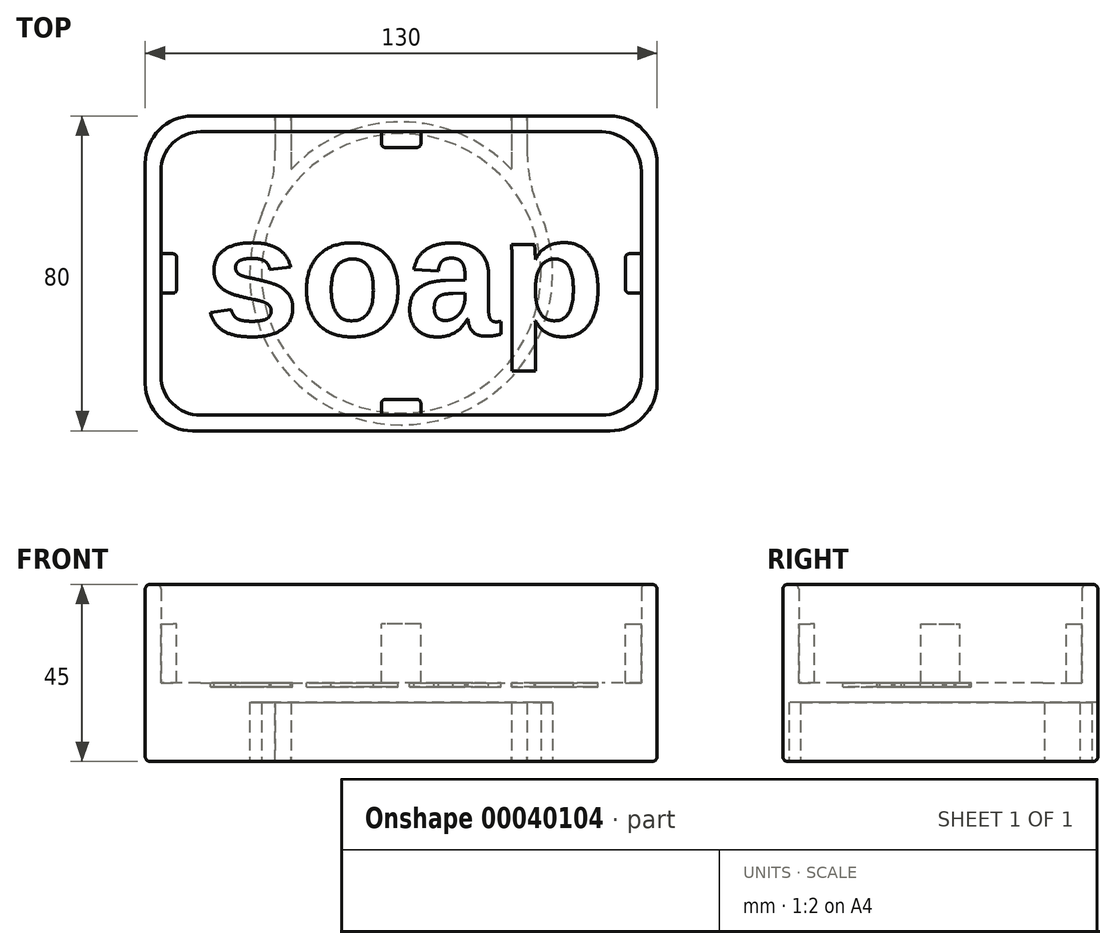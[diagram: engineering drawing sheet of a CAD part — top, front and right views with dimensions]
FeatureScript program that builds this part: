
annotation { "Feature Type Name" : "Feature", "Feature Type Description" : "" }
export const myFeature = defineFeature(function(context is Context, id is Id, definition is map)
    precondition{}
    {
        {
            assignVariable(context, id + "F0", {"name" : "long", "anyValue" : 130});
        }
        {
            assignVariable(context, id + "F1", {"name" : "large", "anyValue" : 80});
        }
        {
            var Q0;
            Q0=qCreatedBy(makeId("Top.planeOp"),FACE);
            var sketch = newSketch(context, id + "F2", { "sketchPlane" : qUnion([Q0])});
            skLineSegment(sketch, "E0.bottom", {"start": v(0, 0) * mm, "end": v(130, 0) * mm});
            skLineSegment(sketch, "E0.top", {"start": v(0, 80) * mm, "end": v(130, 80) * mm});
            skLineSegment(sketch, "E0.left", {"start": v(0, 0) * mm, "end": v(0, 80) * mm});
            skLineSegment(sketch, "E0.right", {"start": v(130, 0) * mm, "end": v(130, 80) * mm});
            skSolve(sketch);
        }
        {
            var Q0;
            Q0 = qSketchRegion(id + "F2", true);
            extrude(context, id + "F3", {"entities" : qUnion([Q0]), "depth" : 20 * mm});
        }
        {
            var Q0;
            Q0=makeQuery(id+"F3.opExtrude","CAP_FACE",FACE,{"disambiguationData":[OSD([sQuery(id+"F2.wireOp",EDGE,"E0.bottom"),sQuery(id+"F2.wireOp",EDGE,"E0.top"),sQuery(id+"F2.wireOp",EDGE,"E0.left"),sQuery(id+"F2.wireOp",EDGE,"E0.right")])],"isStart":true});
            var sketch = newSketch(context, id + "F4", { "sketchPlane" : qUnion([Q0])});
            skPoint(sketch, "E1", {"position": v(65, -80) * mm});
            skPoint(sketch, "E2", {"position": v(65, 0) * mm});
            skLineSegment(sketch, "E3", {"start": v(65, -80) * mm, "end": v(65, 0) * mm, "construction": true});
            skPoint(sketch, "E4", {"position": v(65, -40) * mm});
            skCircle(sketch, "E5", {"center": v(65, -40) * mm, "radius": 35.5 * mm});
            skCircle(sketch, "E6", {"center": v(65, -40) * mm, "radius": 38.5 * mm});
            skPoint(sketch, "E7", {"position": v(93, -80) * mm});
            skLineSegment(sketch, "E8.bottom", {"start": v(93, -80) * mm, "end": v(97, -80) * mm});
            skLineSegment(sketch, "E8.top", {"start": v(93, -61.4) * mm, "end": v(97, -61.4) * mm});
            skLineSegment(sketch, "E8.left", {"start": v(93, -80) * mm, "end": v(93, -61.4) * mm});
            skLineSegment(sketch, "E8.right", {"start": v(97, -80) * mm, "end": v(97, -61.4) * mm});
            skLineSegment(sketch, "E9.bottom", {"start": v(37, -80) * mm, "end": v(33, -80) * mm});
            skLineSegment(sketch, "E9.top", {"start": v(37, -61.4) * mm, "end": v(33, -61.4) * mm});
            skLineSegment(sketch, "E9.left", {"start": v(37, -80) * mm, "end": v(37, -61.4) * mm});
            skLineSegment(sketch, "E9.right", {"start": v(33, -80) * mm, "end": v(33, -61.4) * mm});
            skSolve(sketch);
        }
        {
            var Q0;
            Q0 = qSketchRegion(id + "F4", true);
            extrude(context, id + "F5", {"entities" : qUnion([Q0]), "operationType" : NewBodyOperationType.REMOVE, "oppositeDirection" : true, "depth" : 15 * mm});
        }
        {
            var Q0;
            Q0=makeQuery(id+"F3.opExtrude","CAP_FACE",FACE,{"disambiguationData":[OSD([sQuery(id+"F2.wireOp",EDGE,"E0.bottom"),sQuery(id+"F2.wireOp",EDGE,"E0.top"),sQuery(id+"F2.wireOp",EDGE,"E0.left"),sQuery(id+"F2.wireOp",EDGE,"E0.right")])],"isStart":false});
            var sketch = newSketch(context, id + "F6", { "sketchPlane" : qUnion([Q0])});
            skLineSegment(sketch, "E10.bottom", {"start": v(0, 80) * mm, "end": v(130, 80) * mm});
            skLineSegment(sketch, "E10.top", {"start": v(0, 0) * mm, "end": v(130, 0) * mm});
            skLineSegment(sketch, "E10.left", {"start": v(0, 80) * mm, "end": v(0, 0) * mm});
            skLineSegment(sketch, "E10.right", {"start": v(130, 80) * mm, "end": v(130, 0) * mm});
            skLineSegment(sketch, "E11.bottom", {"start": v(4, 76) * mm, "end": v(126, 76) * mm});
            skLineSegment(sketch, "E11.top", {"start": v(4, 4) * mm, "end": v(126, 4) * mm});
            skLineSegment(sketch, "E11.left", {"start": v(4, 76) * mm, "end": v(4, 4) * mm});
            skLineSegment(sketch, "E11.right", {"start": v(126, 76) * mm, "end": v(126, 4) * mm});
            skSolve(sketch);
        }
        {
            var Q0;
            Q0 = qSketchRegion(id + "F6", true);
            extrude(context, id + "F7", {"entities" : qUnion([Q0]), "operationType" : NewBodyOperationType.ADD, "depth" : 25 * mm});
        }
        {
            var Q0;
            Q0=makeQuery(id+"F7.opExtrude","SWEPT_EDGE",EDGE,{"disambiguationData":[OSD([sQuery(id+"F6.wireOp",EDGE,"E11.bottom"),sQuery(id+"F6.wireOp",EDGE,"E11.left")])]});
            var Q1;
            Q1=makeQuery(id+"F7.opExtrude","SWEPT_EDGE",EDGE,{"disambiguationData":[OSD([sQuery(id+"F6.wireOp",EDGE,"E11.bottom"),sQuery(id+"F6.wireOp",EDGE,"E11.right")])]});
            var Q2;
            Q2=makeQuery(id+"F7.opExtrude","SWEPT_EDGE",EDGE,{"disambiguationData":[OSD([sQuery(id+"F6.wireOp",EDGE,"E11.top"),sQuery(id+"F6.wireOp",EDGE,"E11.right")])]});
            var Q3;
            Q3=makeQuery(id+"F7.opExtrude","SWEPT_EDGE",EDGE,{"disambiguationData":[OSD([sQuery(id+"F6.wireOp",EDGE,"E11.top"),sQuery(id+"F6.wireOp",EDGE,"E11.left")])]});
            fillet(context, id + "F8", {"entities" : qUnion([Q0, Q1, Q2, Q3]), "radius" : 10 * mm, "tangentPropagation" : true, "allowEdgeOverflow" : false});
        }
        {
            var Q0;
            Q0=makeQuery(id+"F7.boolean.opBoolean","MERGE",EDGE,{"derivedFrom":[makeQuery(id+"F3.opExtrude","SWEPT_EDGE",EDGE,{"disambiguationData":[OSD([sQuery(id+"F2.wireOp",EDGE,"E0.top"),sQuery(id+"F2.wireOp",EDGE,"E0.left")])]}),makeQuery(id+"F7.opExtrude","SWEPT_EDGE",EDGE,{"disambiguationData":[OSD([sQuery(id+"F6.wireOp",EDGE,"E10.bottom"),sQuery(id+"F6.wireOp",EDGE,"E10.left")])]})]});
            var Q1;
            Q1=makeQuery(id+"F7.boolean.opBoolean","MERGE",EDGE,{"derivedFrom":[makeQuery(id+"F3.opExtrude","SWEPT_EDGE",EDGE,{"disambiguationData":[OSD([sQuery(id+"F2.wireOp",EDGE,"E0.bottom"),sQuery(id+"F2.wireOp",EDGE,"E0.left")])]}),makeQuery(id+"F7.opExtrude","SWEPT_EDGE",EDGE,{"disambiguationData":[OSD([sQuery(id+"F6.wireOp",EDGE,"E10.top"),sQuery(id+"F6.wireOp",EDGE,"E10.left")])]})]});
            var Q2;
            Q2=makeQuery(id+"F7.boolean.opBoolean","MERGE",EDGE,{"derivedFrom":[makeQuery(id+"F3.opExtrude","SWEPT_EDGE",EDGE,{"disambiguationData":[OSD([sQuery(id+"F2.wireOp",EDGE,"E0.bottom"),sQuery(id+"F2.wireOp",EDGE,"E0.right")])]}),makeQuery(id+"F7.opExtrude","SWEPT_EDGE",EDGE,{"disambiguationData":[OSD([sQuery(id+"F6.wireOp",EDGE,"E10.top"),sQuery(id+"F6.wireOp",EDGE,"E10.right")])]})]});
            var Q3;
            Q3=makeQuery(id+"F7.boolean.opBoolean","MERGE",EDGE,{"derivedFrom":[makeQuery(id+"F3.opExtrude","SWEPT_EDGE",EDGE,{"disambiguationData":[OSD([sQuery(id+"F2.wireOp",EDGE,"E0.top"),sQuery(id+"F2.wireOp",EDGE,"E0.right")])]}),makeQuery(id+"F7.opExtrude","SWEPT_EDGE",EDGE,{"disambiguationData":[OSD([sQuery(id+"F6.wireOp",EDGE,"E10.bottom"),sQuery(id+"F6.wireOp",EDGE,"E10.right")])]})]});
            fillet(context, id + "F9", {"entities" : qUnion([Q0, Q1, Q2, Q3]), "radius" : 12 * mm, "tangentPropagation" : true, "allowEdgeOverflow" : false});
        }
        {
            var Q0;
            Q0=qCreatedBy(makeId("Right.planeOp"),FACE);
            cPlane(context, id + "F10", {"entities" : qUnion([Q0]), "cplaneType" : CPlaneType.OFFSET, "offset" : (getVariable(context, 'long') / 2) * mm, "width" : 150 * mm, "height" : 150 * mm});
        }
        {
            var Q0;
            Q0=qCreatedBy(id+"F10.planeOp",FACE);
            var sketch = newSketch(context, id + "F11", { "sketchPlane" : qUnion([Q0])});
            skLineSegment(sketch, "E12.bottom", {"start": v(4, 20) * mm, "end": v(8, 20) * mm});
            skLineSegment(sketch, "E12.top", {"start": v(4, 35) * mm, "end": v(8, 35) * mm});
            skLineSegment(sketch, "E12.left", {"start": v(4, 20) * mm, "end": v(4, 35) * mm});
            skLineSegment(sketch, "E12.right", {"start": v(8, 20) * mm, "end": v(8, 35) * mm});
            skLineSegment(sketch, "E13.1.0.0", {"start": v(72, 20) * mm, "end": v(72, 35) * mm});
            skLineSegment(sketch, "E13.1.0.1", {"start": v(76, 20) * mm, "end": v(76, 35) * mm});
            skLineSegment(sketch, "E13.1.0.2", {"start": v(72, 20) * mm, "end": v(76, 20) * mm});
            skLineSegment(sketch, "E13.1.0.3", {"start": v(72, 35) * mm, "end": v(76, 35) * mm});
            skLineSegment(sketch, "E13.direction1", {"start": v(4, 20) * mm, "end": v(72, 20) * mm, "construction": true});
            skSolve(sketch);
        }
        {
            var Q0;
            Q0 = qSketchRegion(id + "F11", true);
            extrude(context, id + "F12", {"entities" : qUnion([Q0]), "operationType" : NewBodyOperationType.ADD, "endBound" : BoundingType.SYMMETRIC, "depth" : 10 * mm});
        }
        {
            var Q0;
            Q0=qCreatedBy(makeId("Front.planeOp"),FACE);
            cPlane(context, id + "F13", {"entities" : qUnion([Q0]), "cplaneType" : CPlaneType.OFFSET, "offset" : (getVariable(context, 'large') / 2) * mm, "oppositeDirection" : true, "width" : 150 * mm, "height" : 150 * mm});
        }
        {
            var Q0;
            Q0=qCreatedBy(id+"F13.planeOp",FACE);
            var sketch = newSketch(context, id + "F14", { "sketchPlane" : qUnion([Q0])});
            skLineSegment(sketch, "E14.bottom", {"start": v(4, 20) * mm, "end": v(8, 20) * mm});
            skLineSegment(sketch, "E14.top", {"start": v(4, 35) * mm, "end": v(8, 35) * mm});
            skLineSegment(sketch, "E14.left", {"start": v(4, 20) * mm, "end": v(4, 35) * mm});
            skLineSegment(sketch, "E14.right", {"start": v(8, 20) * mm, "end": v(8, 35) * mm});
            skLineSegment(sketch, "E15.1.0.0", {"start": v(122, 20) * mm, "end": v(126, 20) * mm});
            skLineSegment(sketch, "E15.1.0.1", {"start": v(122, 35) * mm, "end": v(126, 35) * mm});
            skLineSegment(sketch, "E15.1.0.2", {"start": v(122, 20) * mm, "end": v(122, 35) * mm});
            skLineSegment(sketch, "E15.1.0.3", {"start": v(126, 20) * mm, "end": v(126, 35) * mm});
            skLineSegment(sketch, "E15.direction1", {"start": v(4, 20) * mm, "end": v(122, 20) * mm, "construction": true});
            skSolve(sketch);
        }
        {
            var Q0;
            Q0 = qSketchRegion(id + "F14", true);
            extrude(context, id + "F15", {"entities" : qUnion([Q0]), "operationType" : NewBodyOperationType.ADD, "endBound" : BoundingType.SYMMETRIC, "depth" : 10 * mm});
        }
        {
            var Q0;
            Q0=makeQuery(id+"F12.opExtrude","CAP_EDGE",EDGE,{"disambiguationData":[OSD([sQuery(id+"F11.wireOp",EDGE,"E13.1.0.0")])],"isStart":true});
            var Q1;
            Q1=makeQuery(id+"F12.opExtrude","CAP_EDGE",EDGE,{"disambiguationData":[OSD([sQuery(id+"F11.wireOp",EDGE,"E13.1.0.0")])],"isStart":false});
            var Q2;
            {var subQ0=sQuery(id+"F6.wireOp",EDGE,"E11.bottom");Q2=makeQuery(id+"F12.boolean.opBoolean","SPLIT",EDGE,{"disambiguationData":[TD([makeQuery(id+"F8.opFillet","BLEND_FACE",FACE,{"disambiguationData":[OSD([subQ0,sQuery(id+"F6.wireOp",EDGE,"E11.left")])]})])],"derivedFrom":makeQuery(id+"F7.opExtrude","CAP_EDGE",EDGE,{"disambiguationData":[OSD([subQ0])],"isStart":true})});}
            var Q3;
            Q3=makeQuery(id+"F12.opExtrude","CAP_EDGE",EDGE,{"disambiguationData":[OSD([sQuery(id+"F11.wireOp",EDGE,"E13.1.0.2")])],"isStart":true});
            var Q4;
            {var subQ0=sQuery(id+"F6.wireOp",EDGE,"E11.bottom");Q4=makeQuery(id+"F12.boolean.opBoolean","SPLIT",EDGE,{"disambiguationData":[TD([makeQuery(id+"F8.opFillet","BLEND_FACE",FACE,{"disambiguationData":[OSD([subQ0,sQuery(id+"F6.wireOp",EDGE,"E11.right")])]})])],"derivedFrom":makeQuery(id+"F7.opExtrude","CAP_EDGE",EDGE,{"disambiguationData":[OSD([subQ0])],"isStart":true})});}
            var Q5;
            Q5=makeQuery(id+"F15.opExtrude","SWEPT_EDGE",EDGE,{"disambiguationData":[OSD([sQuery(id+"F14.wireOp",EDGE,"E15.1.0.0"),sQuery(id+"F14.wireOp",EDGE,"E15.1.0.2")])]});
            var Q6;
            Q6=makeQuery(id+"F15.opExtrude","CAP_EDGE",EDGE,{"disambiguationData":[OSD([sQuery(id+"F14.wireOp",EDGE,"E15.1.0.2")])],"isStart":true});
            var Q7;
            Q7=makeQuery(id+"F15.opExtrude","CAP_EDGE",EDGE,{"disambiguationData":[OSD([sQuery(id+"F14.wireOp",EDGE,"E15.1.0.2")])],"isStart":false});
            var Q8;
            {var subQ0=sQuery(id+"F6.wireOp",EDGE,"E11.right");Q8=makeQuery(id+"F15.boolean.opBoolean","SPLIT",EDGE,{"disambiguationData":[TD([makeQuery(id+"F8.opFillet","BLEND_FACE",FACE,{"disambiguationData":[OSD([sQuery(id+"F6.wireOp",EDGE,"E11.top"),subQ0])]})])],"derivedFrom":makeQuery(id+"F7.opExtrude","CAP_EDGE",EDGE,{"disambiguationData":[OSD([subQ0])],"isStart":true})});}
            var Q9;
            Q9=makeQuery(id+"F12.opExtrude","SWEPT_EDGE",EDGE,{"disambiguationData":[OSD([sQuery(id+"F11.wireOp",EDGE,"E12.bottom"),sQuery(id+"F11.wireOp",EDGE,"E12.right")])]});
            var Q10;
            Q10=makeQuery(id+"F12.opExtrude","CAP_EDGE",EDGE,{"disambiguationData":[OSD([sQuery(id+"F11.wireOp",EDGE,"E12.bottom")])],"isStart":false});
            var Q11;
            {var subQ0=sQuery(id+"F6.wireOp",EDGE,"E11.top");Q11=makeQuery(id+"F12.boolean.opBoolean","SPLIT",EDGE,{"disambiguationData":[TD([makeQuery(id+"F8.opFillet","BLEND_FACE",FACE,{"disambiguationData":[OSD([subQ0,sQuery(id+"F6.wireOp",EDGE,"E11.left")])]})])],"derivedFrom":makeQuery(id+"F7.opExtrude","CAP_EDGE",EDGE,{"disambiguationData":[OSD([subQ0])],"isStart":true})});}
            var Q12;
            Q12=makeQuery(id+"F15.opExtrude","SWEPT_EDGE",EDGE,{"disambiguationData":[OSD([sQuery(id+"F14.wireOp",EDGE,"E14.bottom"),sQuery(id+"F14.wireOp",EDGE,"E14.right")])]});
            var Q13;
            Q13=makeQuery(id+"F15.opExtrude","CAP_EDGE",EDGE,{"disambiguationData":[OSD([sQuery(id+"F14.wireOp",EDGE,"E14.bottom")])],"isStart":true});
            var Q14;
            Q14=makeQuery(id+"F15.opExtrude","CAP_EDGE",EDGE,{"disambiguationData":[OSD([sQuery(id+"F14.wireOp",EDGE,"E14.bottom")])],"isStart":false});
            var Q15;
            Q15=makeQuery(id+"F12.opExtrude","CAP_EDGE",EDGE,{"disambiguationData":[OSD([sQuery(id+"F11.wireOp",EDGE,"E12.bottom")])],"isStart":true});
            var Q16;
            Q16=makeQuery(id+"F12.opExtrude","CAP_EDGE",EDGE,{"disambiguationData":[OSD([sQuery(id+"F11.wireOp",EDGE,"E12.right")])],"isStart":false});
            var Q17;
            Q17=makeQuery(id+"F12.opExtrude","CAP_EDGE",EDGE,{"disambiguationData":[OSD([sQuery(id+"F11.wireOp",EDGE,"E12.right")])],"isStart":true});
            var Q18;
            Q18=makeQuery(id+"F15.opExtrude","CAP_EDGE",EDGE,{"disambiguationData":[OSD([sQuery(id+"F14.wireOp",EDGE,"E14.right")])],"isStart":false});
            var Q19;
            Q19=makeQuery(id+"F15.opExtrude","CAP_EDGE",EDGE,{"disambiguationData":[OSD([sQuery(id+"F14.wireOp",EDGE,"E14.right")])],"isStart":true});
            var Q20;
            Q20=makeQuery(id+"F15.opExtrude","CAP_EDGE",EDGE,{"disambiguationData":[OSD([sQuery(id+"F14.wireOp",EDGE,"E14.right")])],"isStart":true});
            fillet(context, id + "F16", {"entities" : qUnion([Q0, Q1, Q2, Q3, Q4, Q5, Q6, Q7, Q8, Q9, Q10, Q11, Q12, Q13, Q14, Q15, Q16, Q17, Q18, Q19, Q20]), "radius" : 1 * mm, "tangentPropagation" : true, "allowEdgeOverflow" : false});
        }
        {
            var Q0;
            Q0=makeQuery(id+"F7.opExtrude","CAP_EDGE",EDGE,{"disambiguationData":[OSD([sQuery(id+"F6.wireOp",EDGE,"E10.top")])],"isStart":false});
            var Q1;
            Q1=makeQuery(id+"F7.opExtrude","CAP_EDGE",EDGE,{"disambiguationData":[OSD([sQuery(id+"F6.wireOp",EDGE,"E11.bottom")])],"isStart":false});
            var Q2;
            Q2=makeQuery(id+"F3.opExtrude","CAP_EDGE",EDGE,{"disambiguationData":[OSD([sQuery(id+"F2.wireOp",EDGE,"E0.bottom")])],"isStart":true});
            var Q3;
            {var subQ0=sQuery(id+"F2.wireOp",EDGE,"E0.top");Q3=makeQuery(id+"F5.boolean.opBoolean","SPLIT",EDGE,{"disambiguationData":[TD([makeQuery(id+"F5.opExtrude","SWEPT_FACE",FACE,{"disambiguationData":[OSD([sQuery(id+"F4.wireOp",EDGE,"E8.left")])]})])],"derivedFrom":makeQuery(id+"F3.opExtrude","CAP_EDGE",EDGE,{"disambiguationData":[OSD([subQ0])],"isStart":true})});}
            var Q4;
            Q4=makeQuery(id+"F5.boolean.opBoolean","COPY",EDGE,{"derivedFrom":makeQuery(id+"F5.opExtrude","CAP_EDGE",EDGE,{"disambiguationData":[OSD([sQuery(id+"F4.wireOp",EDGE,"E5")])],"isStart":true})});
            fillet(context, id + "F17", {"entities" : qUnion([Q0, Q1, Q2, Q3, Q4]), "radius" : 1.2 * mm, "tangentPropagation" : true, "allowEdgeOverflow" : false});
        }
        {
            var Q0;
            Q0=makeQuery(id+"F3.opExtrude","CAP_FACE",FACE,{"disambiguationData":[OSD([sQuery(id+"F2.wireOp",EDGE,"E0.bottom"),sQuery(id+"F2.wireOp",EDGE,"E0.top"),sQuery(id+"F2.wireOp",EDGE,"E0.left"),sQuery(id+"F2.wireOp",EDGE,"E0.right")])],"isStart":false});
            var sketch = newSketch(context, id + "F18", { "sketchPlane" : qUnion([Q0])});
            skText(sketch, "E16", { "text": "soap", "fontName": "Arimo-Bold.ttf"});
            skPoint(sketch, "E17", {"position": v(15, 40) * mm});
            const initialGuessF18  = {"E16": [0.015, 0.0243, 1, 0, 0.0314]};
            skSetInitialGuess(sketch, initialGuessF18);
            skSolve(sketch);
        }
        {
            var Q0;
            Q0 = qSketchRegion(id + "F18", true);
            extrude(context, id + "F19", {"entities" : qUnion([Q0]), "operationType" : NewBodyOperationType.REMOVE, "oppositeDirection" : true, "depth" : 1 * mm});
        }
        {
            var Q0;
            Q0=makeQuery(id+"F5.boolean.opBoolean","COPY",EDGE,{"derivedFrom":makeQuery(id+"F5.opExtrude","SWEPT_EDGE",EDGE,{"disambiguationData":[OSD([sQuery(id+"F4.wireOp",EDGE,"E6"),sQuery(id+"F4.wireOp",EDGE,"E9.top"),sQuery(id+"F4.wireOp",EDGE,"E9.right")])]})});
            var Q1;
            Q1=makeQuery(id+"F5.boolean.opBoolean","COPY",EDGE,{"derivedFrom":makeQuery(id+"F5.opExtrude","SWEPT_EDGE",EDGE,{"disambiguationData":[OSD([sQuery(id+"F4.wireOp",EDGE,"E6"),sQuery(id+"F4.wireOp",EDGE,"E8.top"),sQuery(id+"F4.wireOp",EDGE,"E8.right")])]})});
            fillet(context, id + "F20", {"entities" : qUnion([Q0, Q1]), "radius" : 40 * mm, "tangentPropagation" : true, "allowEdgeOverflow" : false});
        }
    });
